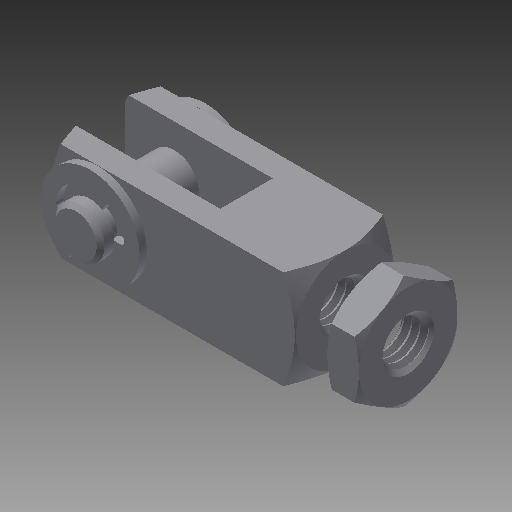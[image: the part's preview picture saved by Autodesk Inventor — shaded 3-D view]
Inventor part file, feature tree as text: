
AUTODESK INVENTOR PART (.ipt)
format: ipt  version: 2017 (Build 210142000, 142)  size: 936,448 bytes
history: native  units: in
note: dims shown in document units (in); Inventor stores cm internally (conversion verified against a paired STEP export)
features: imported_body x5, other x4, revolve x1, mirror x1
ambient origin geometry x8: Origin, YZ Plane, XZ Plane, XY Plane, X Axis, Y Axis, Z Axis, Center Point
bodies: Body1 (feature_tree), Body2 (feature_tree), Body3 (feature_tree), Body4 (feature_tree), Body5 (feature_tree)
feature tree (11):
  other  "Cut-Extrude5"
  other  "cylinder_9-16bore_clevis1"
  revolve  "Revolve1"  [1 undecoded]
  other  "Boss-Extrude2"
  mirror  "Mirror1"
  other  "Cut-Extrude9"
  imported_body  "Base1"
  imported_body  "Base2"
  imported_body  "Base3"
  imported_body  "Base4"
  imported_body  "Base5"
note: 1 required parameter value undecoded (feature->parameter linkage not recoverable at this tier; creation-order binding heuristic only, values carry confidence <= 0.55)
